# Revit family: Walkway_Kattsafe_Guardrail1Side
name_source: partatom
category: Specialty Equipment
units: mm (PartAtom-declared; Revit-internal decimal feet)

## family parameters
Cut with Voids When Loaded = No
Enable Cutting in Views = No
Maintain Annotation Orientation = No
OmniClass Number = 23.13.41.19
Part Type = Normal
Room Calculation Point = No
Round Connector Dimension = Use Diameter
Shared = No

## types (2) — shared parameters
Assembly Code = E1090100
Description = Kattsafe guardrail systems are the preferred method of safe access across roofs and areas close to a fall edge. The system requires no specialist PPE, personnel or training to safely prevent a fall with a walkway to designate a safe path of access across the roof surface.
ElementType = Roof Walkway
Export Type to IFC As = IfcBuildingElementProxy
GuardrailHeight = 985 mm
HandrailAngledOffsetHeight = -57 mm  [stored -0.187008 ft]
HandrailClosureAngledOffsetHeight = -532 mm  [stored -1.74541 ft]
IfcExportAs = IfcBuildingElementProxy
IfcExportType = USERDEFINED
Manufacturer = Kattsafe®
ManufacturerOverallHeight = 1040 mm  [stored 3.41207 ft]
ManufacturerOverallHeightCalc = 1040 mm  [stored 3.41207 ft]
ManufacturerOverallWidth = 1000 mm  [stored 3.28084 ft]
ManufacturerSpecCode = GW4
ManufacturerURLProductSpecific = https://kattsafe.com.au
Material = Aluminum_Kattsafe_Satin
Model = GW4
ModifiedIssue = 20240430 $
PostsHeight = 998 mm  [stored 3.27428 ft]
PostsMaxSpacingLength = 2000 mm  [stored 6.56168 ft]
ToeboardAngledOffsetHeight = 63 mm  [stored 0.206693 ft]
Type Comments = Walkway - Guardrail 1 Side - Across Slope
Type IFC Predefined Type = USERDEFINED
URL = https://kattsafe.com.au
Uniclass2015Code = Pr_40_70_75_96
Uniclass2015Title = Working platforms
Uniclass2015Version = Products v1.23
WalkwayMaterial = Aluminum_Kattsafe_Mesh_Walkway
WalkwayWidth = 600 mm
zero-valued in all types: Default Elevation

## per-type parameters (varying)
| type | AcrossSlope |
| Across Slope (GW4) | Yes |
| Along Slope (GW4) | No |

note: [stored X ft] marks values corroborated as IEEE doubles in the binary element streams (Revit-internal decimal feet)

## geometry (parser evidence)
native form markers: Sweep x16
no freeform markers — native parametric forms only
